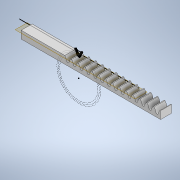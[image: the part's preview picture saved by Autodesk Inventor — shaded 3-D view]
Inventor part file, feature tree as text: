
AUTODESK INVENTOR PART (.ipt)
format: ipt  version: 2021 (Build 250183000, 183)  size: 179,200 bytes
history: native  units: mm
features: extrude x2, pattern_linear x1, plane x1, sketch x1
ambient origin geometry x8: Origin, YZ Plane, XZ Plane, XY Plane, X Axis, Y Axis, Z Axis, Center Point
bodies: Body1 (feature_tree)
feature tree (5):
  extrude  "Extrusion4"  Depth=7.0mm
  extrude  "Extrusion5"  Depth=40.0mm
  pattern_linear  "Rectangular Pattern1"  Spacing1=10.0mm  [1 undecoded]
  plane  "Work Plane1"
  sketch  "Sketch4"  dims[d10=127.7mm d11=7.0mm d12=40.0mm d13=10.0mm d14=0.0mm d15=10.0mm d16=0.0mm d17=150.0mm d19=6.285714mm d7=1.0mm d8=1.0mm d9=1.0mm d18=0.375mm]
note: 1 required parameter value undecoded (feature->parameter linkage not recoverable at this tier; creation-order binding heuristic only, values carry confidence <= 0.55)
